# Revit family: LEGRAND_NON INTERLOCKED SOCKETS_FLUSH MOUNTED_IP44_110
name_source: partatom
category: Installations électriques
revit_build: Autodesk Revit 2018 (Build: 20170223_1515(x64)
units: mm (PartAtom-declared; Revit-internal decimal feet)

## family parameters
Conserver l'orientation des annotations = Non
Cote de connecteur circulaire = Utiliser le diamètre
Couper avec des vides une fois chargée = Non
Hôte = Face
Partagée = Non
Point de calcul de pièce = Non
Type d'élément = Normal

## types (4) — shared parameters
Description = international standard socket for flush or surface mounting with accessory allows the connection of power devices
Elévation par défaut = 1000 mm  [stored 3.28084 ft]
Fabricant = Legrand
Flush E or Surface mounting S = flush and surface mounting
General Conditions of Use = https://export.legrand.com
Maximum installation temperature = 40°C
Maximum use temperature = 100°C
Minimum installation temperature = -20°C
Minimum use temperature = -50°C
Number of poles = 3
Position of earth h = 4
Standard IEC or NFC = IEC
Tension V = 110 V  50/60 Hz yellow
characteristic color = yellow
connecting type = screw terminals
halogen free = Oui
protection class IP = IP44

## per-type parameters (varying)
| type | Dia bouchon | Modèle | RAY BOUCHON | Ray | depth for flush mounting mm | depth mm | h1 | height mm | horizontal fixing distance mm | intensity A | material of box | resistance to chocks IK | vertical fixing distance mm | width mm |
| panel mounting socket single fixing center Hypra  IP44   16 A  110 V   2P+E  plast | 50 mm | 051919 | 25 mm  [stored 0.082021 ft] | 25 mm  [stored 0.082021 ft] | 41 mm | 73 mm  [stored 0.239501 ft] | 50 mm | 84 mm | 70 mm | 16 A | plastic | 09 | 70 mm | 84 mm |
| panel mounting socket  Hypra  IP44   16 A  110 V   2P+E  plast | 50 mm | 051920 | 25 mm  [stored 0.082021 ft] | 25 mm  [stored 0.082021 ft] | 41 mm | 81 mm  [stored 0.265748 ft] | 50 mm | 84 mm | 70 mm | 16 A | plastic | 09 | 70 mm | 84 mm |
| panel mounting socket  Hypra  IP44   32 A  110 V   2P+E  plast | 50 mm | 051921 | 25 mm  [stored 0.082021 ft] | 25 mm  [stored 0.082021 ft] | 50 mm | 103 mm | 50 mm | 84 mm | 70 mm | 32 A | plastic | 09 | 70 mm | 83 mm |
| panel mounting socket  Hypra  IP44   16 A  110 V   2P+E  métal | 38 mm | 051930 | 19 mm | 19 mm | 41 mm | 81 mm  [stored 0.265748 ft] | 43 mm | 72 mm | 52 mm | 16 A | metal | 10 | 60 mm | 64 mm |

note: [stored X ft] marks values corroborated as IEEE doubles in the binary element streams (Revit-internal decimal feet)
